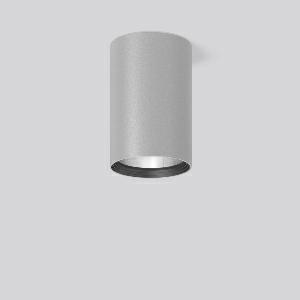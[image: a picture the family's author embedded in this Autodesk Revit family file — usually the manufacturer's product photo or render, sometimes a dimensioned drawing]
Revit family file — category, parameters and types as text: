
# Revit family: heledon_maxi_a_931217_004_2_fbff
name_source: partatom
category: Lighting Fixtures
units: mm (PartAtom-declared; Revit-internal decimal feet)

## family parameters
Cut with Voids When Loaded = No
Host = Face
Light Source = No
Part Type = Normal
Room Calculation Point = No
Round Connector Dimension = Use Diameter
Shared = No

## types (1)
- HELEDON maxi A (1 x LED Modul 927, 3150 lm, 2700)
    Apparent Load = 25 VA
    Approval mark = CE
    CIE Flux Codes = 100 100 100 100 100
    Color Rendering = 92
    Color Temperature = 2700
    Default Elevation = 1800 mm
    Description = Series: HELEDON maxi
Cylindrical surface-mounted downlight. Housing: die-cast aluminium, powder-coated. Internal ceiling frame polycarbonate with bayonet mounting. Black plastic ring and recessed LED to prevent glare from the side. Optical assembly with reflector made of MIRO-Silver with 98% total light reflection for outstanding efficiency - can be changed without tools. Best colour rendering index Ra>90. Suitable for Ceiling mounting. Easy installation with a separate ceiling frame with bayonet mounting and plug connection. Driver integrated. Connected via plug-in connector. High quality converter without flickering and stroboscopic effect. The following accessories can be mounted without use of tools: interchangeable lenses, decorative glasses, honeycomb louvre, clear and frosted diffusers, white interchangeable plastic ring. 
Colour: silver
Diameter: 123 mm
Height: 183 mm
Lamp: LED
Socket: without socket
Colour temperature: 2700K
Colour rendering index (CRI): 92
System power: 25 W
Rated luminous flux: 3150 lm
Luminous efficiency: 126 lm/W
Control gear: Regulated power supply
Protection class: I
Type of protection: IP 20
    Height = 183 mm
    Lamp = 1 x LED Modul 927
    Lamp Light Flux = 3150 lm
    Lamp count = 1
    Length = 123 mm
    Lifetime = 50000 h
    Luminous efficacy = 126 lm/W
    Manufacturer = RZB
    ModVariant = No
    Model = 931217.004.2
    Mounting Place = Ceiling
    Mounting Type = Surface mounted
    Number of Poles = 1
    OnlyDefault = Yes
    Power Factor = 1
    Product Name = HELEDON maxi A
    Product group = Surface mounted downlights
    ProductGroupID = 302
    Protection Class = Protection class I
    Protection Degree = IP 20
    RLX_Detail_Level = 1
    RLX_Emergency_Light_Flux = 0 lm
    RLX_Emergency_Type = 0
    RLX_Emergency_Type_DB = No
    RlxData = <blob elided: 98029 chars, md5=ec4c1a47>
    Socket = socket
    Standby Power = 0 W
    System Light Flux = 3150 lm
    System Power = 25 W
    Type Comments = Product without accessories
    Type Image = 931192.004.jpg
    URL = http://relux.com
    VarID = ---
    Voltage = 230 V
    Voltage Range = 220-240 V
    Weight = 0.00 kg
    Width = 0 mm  [stored 0 ft]

note: [stored X ft] marks values corroborated as IEEE doubles in the binary element streams (Revit-internal decimal feet)

## geometry (parser evidence)
native form markers: Blend x4, Sweep x11
no freeform markers — native parametric forms only
